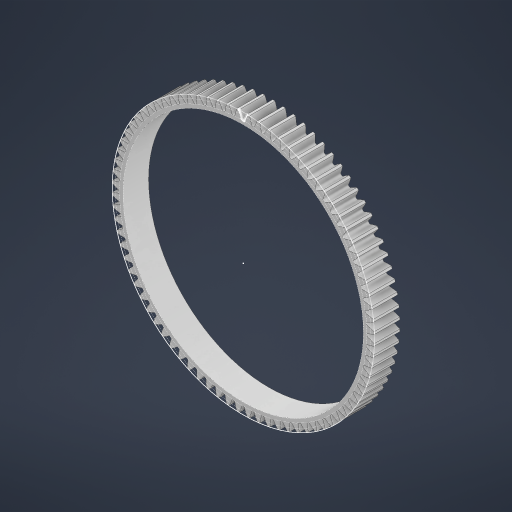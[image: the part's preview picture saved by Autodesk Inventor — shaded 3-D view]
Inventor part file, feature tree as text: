
AUTODESK INVENTOR PART (.ipt)
format: ipt  version: 2023.2 (Build 272271000, 271)  size: 532,992 bytes
history: native  units: mm
features: extrude x3, sketch x2, pattern_circular x1
ambient origin geometry x8: Origin, YZ Plane, XZ Plane, XY Plane, X Axis, Y Axis, Z Axis, Center Point
bodies: Solid1 (feature_tree)
feature tree (6):
  sketch  "Sketch1"  dims[d0=8.0mm d1=0.0mm]
  extrude  "Extrusion1"  TaperAngle=0.0deg  [1 undecoded]
  extrude  "Extrusion2"  Depth=800.0mm TaperAngle=360.0deg
  pattern_circular  "Circular Pattern1"  [2 undecoded]
  extrude  "Extrusion3"  [1 undecoded]
  sketch  "Sketch2"  dims[d2=0.0mm d3=0.0mm d4=800.0mm d5=360.0deg d7=0.0mm d8=0.0mm]
note: 4 required parameter values undecoded (feature->parameter linkage not recoverable at this tier; creation-order binding heuristic only, values carry confidence <= 0.55)
